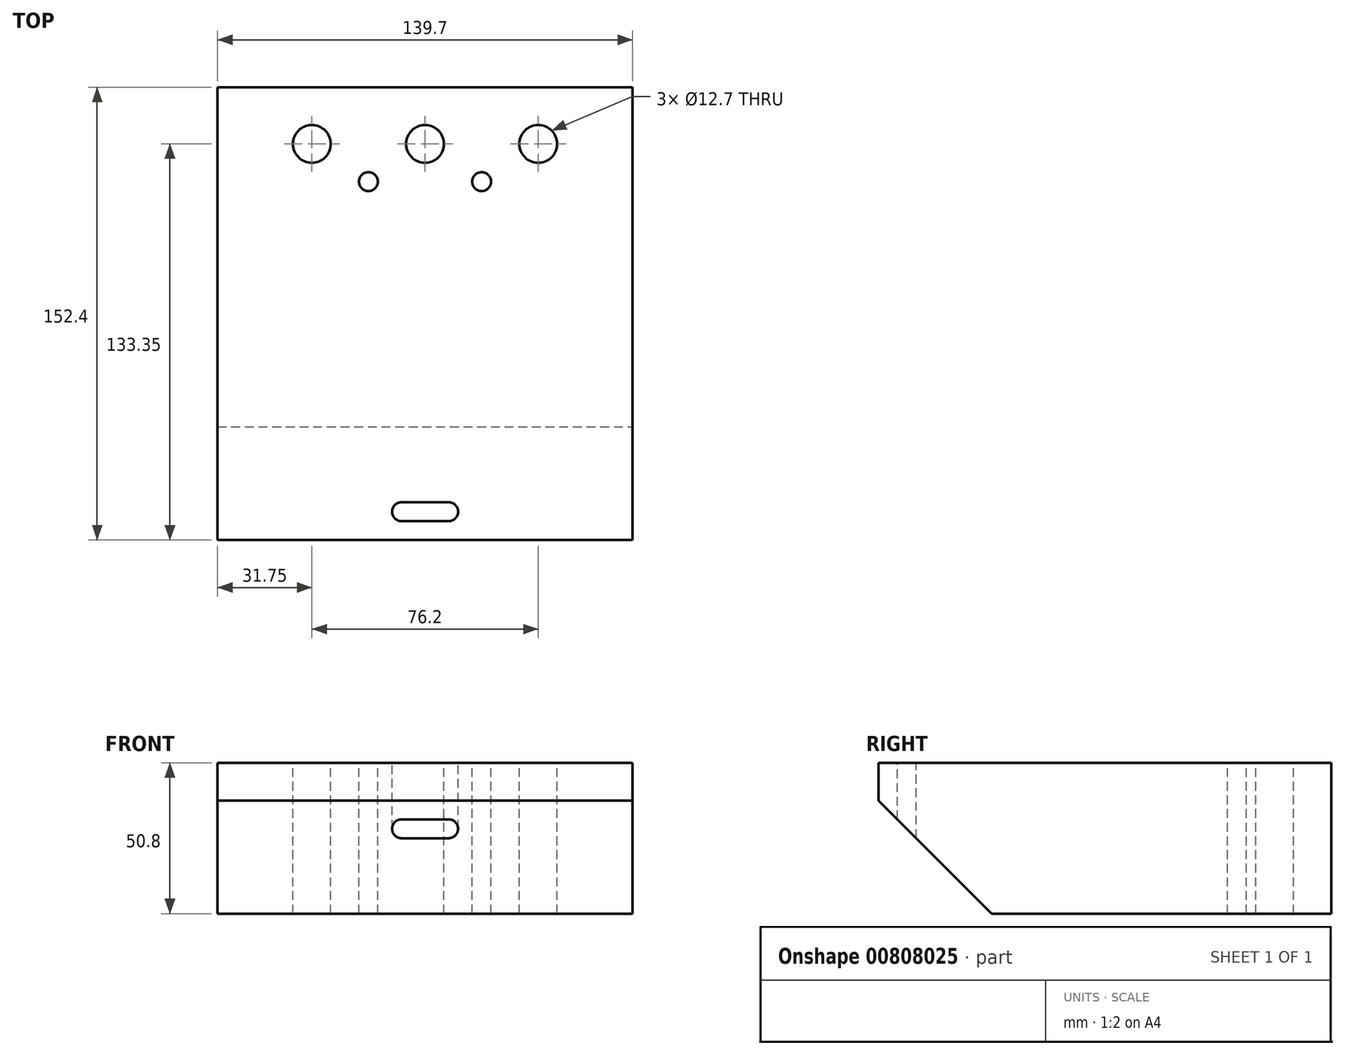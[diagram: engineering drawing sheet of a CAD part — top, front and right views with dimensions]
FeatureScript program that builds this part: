
annotation { "Feature Type Name" : "Feature", "Feature Type Description" : "" }
export const myFeature = defineFeature(function(context is Context, id is Id, definition is map)
    precondition{}
    {
        {
            var Q0;
            Q0=qCreatedBy(makeId("Top.planeOp"),FACE);
            var sketch = newSketch(context, id + "F0", { "sketchPlane" : qUnion([Q0])});
            skLineSegment(sketch, "E0.bottom", {"start": v(69.85, -76.2) * mm, "end": v(-69.85, -76.2) * mm});
            skLineSegment(sketch, "E0.top", {"start": v(69.85, 76.2) * mm, "end": v(-69.85, 76.2) * mm});
            skLineSegment(sketch, "E0.left", {"start": v(69.85, -76.2) * mm, "end": v(69.85, 76.2) * mm});
            skLineSegment(sketch, "E0.right", {"start": v(-69.85, -76.2) * mm, "end": v(-69.85, 76.2) * mm});
            skPoint(sketch, "E0.middle", {"position": v(0, 0) * mm});
            skSolve(sketch);
        }
        {
            var Q0;
            Q0 = qSketchRegion(id + "F0", true);
            extrude(context, id + "F1", {"entities" : qUnion([Q0]), "oppositeDirection" : true, "depth" : 50.8 * mm, "offsetDistance" : 25.4 * mm});
        }
        {
            var Q0;
            Q0=makeQuery(id+"F1.opExtrude","CAP_FACE",FACE,{"disambiguationData":[OSD([sQuery(id+"F0.wireOp",EDGE,"E0.bottom"),sQuery(id+"F0.wireOp",EDGE,"E0.top"),sQuery(id+"F0.wireOp",EDGE,"E0.left"),sQuery(id+"F0.wireOp",EDGE,"E0.right")])],"isStart":true});
            var sketch = newSketch(context, id + "F2", { "sketchPlane" : qUnion([Q0])});
            skLineSegment(sketch, "E1.0", {"start": v(69.85, -76.2) * mm, "end": v(-69.85, -76.2) * mm});
            skLineSegment(sketch, "E2.0", {"start": v(7.94, -69.85) * mm, "end": v(-7.94, -69.85) * mm});
            skLineSegment(sketch, "E3.0", {"start": v(7.94, -63.5) * mm, "end": v(-7.94, -63.5) * mm});
            skArc(sketch, "E4", {"start": v(-7.94, -63.5) * mm, "mid": v(-11.11, -66.68) * mm, "end": v(-7.94, -69.85) * mm});
            skArc(sketch, "E5", {"start": v(7.94, -69.85) * mm, "mid": v(11.11, -66.68) * mm, "end": v(7.94, -63.5) * mm});
            skCircle(sketch, "E6", {"center": v(0, 57.15) * mm, "radius": 6.35 * mm});
            skCircle(sketch, "E7", {"center": v(-38.1, 57.15) * mm, "radius": 6.35 * mm});
            skCircle(sketch, "E8", {"center": v(38.1, 57.15) * mm, "radius": 6.35 * mm});
            skLineSegment(sketch, "E9", {"start": v(-38.1, 57.15) * mm, "end": v(0, 57.15) * mm});
            skLineSegment(sketch, "E10", {"start": v(38.1, 57.15) * mm, "end": v(0, 57.15) * mm});
            skLineSegment(sketch, "E11", {"start": v(-19.05, 57.15) * mm, "end": v(-19.05, 44.45) * mm});
            skLineSegment(sketch, "E12", {"start": v(19.05, 57.15) * mm, "end": v(19.05, 44.45) * mm});
            skCircle(sketch, "E13", {"center": v(-19.05, 44.45) * mm, "radius": 3.18 * mm});
            skCircle(sketch, "E14", {"center": v(19.05, 44.45) * mm, "radius": 3.18 * mm});
            skSolve(sketch);
        }
        {
            var Q0;
            Q0 = qSketchRegion(id + "F2", true);
            extrude(context, id + "F3", {"entities" : qUnion([Q0]), "operationType" : NewBodyOperationType.REMOVE, "endBound" : BoundingType.THROUGH_ALL, "oppositeDirection" : true, "depth" : 25.4 * mm, "offsetDistance" : 25.4 * mm});
        }
        {
            var Q0;
            Q0=makeQuery(id+"F1.opExtrude","SWEPT_FACE",FACE,{"disambiguationData":[OSD([sQuery(id+"F0.wireOp",EDGE,"E0.left")])]});
            var sketch = newSketch(context, id + "F4", { "sketchPlane" : qUnion([Q0])});
            skLineSegment(sketch, "E15.1", {"start": v(-76.2, -50.8) * mm, "end": v(-76.2, -12.7) * mm});
            skLineSegment(sketch, "E16", {"start": v(-76.2, -12.7) * mm, "end": v(-38.1, -50.8) * mm});
            skLineSegment(sketch, "E17", {"start": v(-76.2, -50.8) * mm, "end": v(-38.1, -50.8) * mm});
            skPoint(sketch, "E18.orphan", {"position": v(-76.2, 0) * mm});
            skSolve(sketch);
        }
        {
            var Q0;
            Q0 = qSketchRegion(id + "F4", true);
            extrude(context, id + "F5", {"entities" : qUnion([Q0]), "operationType" : NewBodyOperationType.REMOVE, "endBound" : BoundingType.THROUGH_ALL, "oppositeDirection" : true, "depth" : 25.4 * mm, "offsetDistance" : 25.4 * mm});
        }
    });
